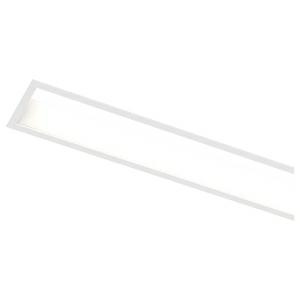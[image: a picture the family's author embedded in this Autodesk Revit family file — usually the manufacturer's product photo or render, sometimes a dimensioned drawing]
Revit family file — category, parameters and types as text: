
# Revit family: groove_l_900_eb_led_16w_1023lm_3000k_cri80_230-1990_bb02
name_source: partatom
category: Leuchten
revit_build: Autodesk Revit 2016 (Build: 20190508_0715(x64)
units: mm (PartAtom-declared; Revit-internal decimal feet)

## family parameters
Basisbauteil = Fläche
Beim Laden mit Abzugskörper schneiden = Nein
Bemaßung runder Anschluss = Durchmesser verwenden
Gemeinsam genutzt = Nein
Lichtquelle = Nein
Raumberechnungspunkt = Nein
Teiletyp = Normal

## types (1)
- 230-1990- (3 x LED, 710 lm, 5.1 W, 3000K)
    Beschreibung = The recessed luminaire GROOVE from the familiy GROOVE consists of aluminum-extruded profile. Charming SOFT-EDGE design ensure unparalleled styling. The ballast is integrated and allows for an operation with 220-240V (50.60Hz). GROOVE (# 230-1990) ist not dimmable (on/off). The luminaire with direct illumination and corresponds to protection class SK1 at IP20.
    CIE Flux Codes = 59 87 97 100 49
    Color Rendering = 1B/80…89
    Color Temperature = 3000K
    Height = 0 mm  [stored 0 ft]
    Hersteller = Prolicht
    Lamp Light Flux = 710 lm
    Lamp Power = 5.1 W
    Lamp count = 3
    Lampe = 3 x LED
    Length = 900 mm
    Luminous efficacy = 67 lm/W
    ModVariant = Nein
    Modell = 230-1990
    Mounting Place = Ceiling
    Mounting Type = Recessed
    Number of Poles = 1
    OnlyDefault = Ja
    Power Factor = 1
    Product Name = GROOVE L=900 EB LED 16W 1023lm 3000K CRI80
    Product group = Recessed profile lights
    ProductGroupID = 423
    Protection Class = Protection class
    Protection Degree = Degree of protection
    RLX_Detail_Level = 1
    RlxData = <blob elided: 168065 chars, md5=1d826c1b>
    Scheinlast = 15 VA
    Socket = socket
    Standby Power = 0 W
    System Light Flux = 1027 lm
    System Power = 15 W
    Typenbild = 230-1990.jpg
    URL = http://relux.com
    VarID = 230-1990-
    Voltage = 0 V
    Vorgabe-Ansicht = 1800 mm
    Weight = 0.00 kg
    Width = 92 mm

note: [stored X ft] marks values corroborated as IEEE doubles in the binary element streams (Revit-internal decimal feet)

## geometry (parser evidence)
native form markers: Blend x4, Sweep x14
no freeform markers — native parametric forms only
